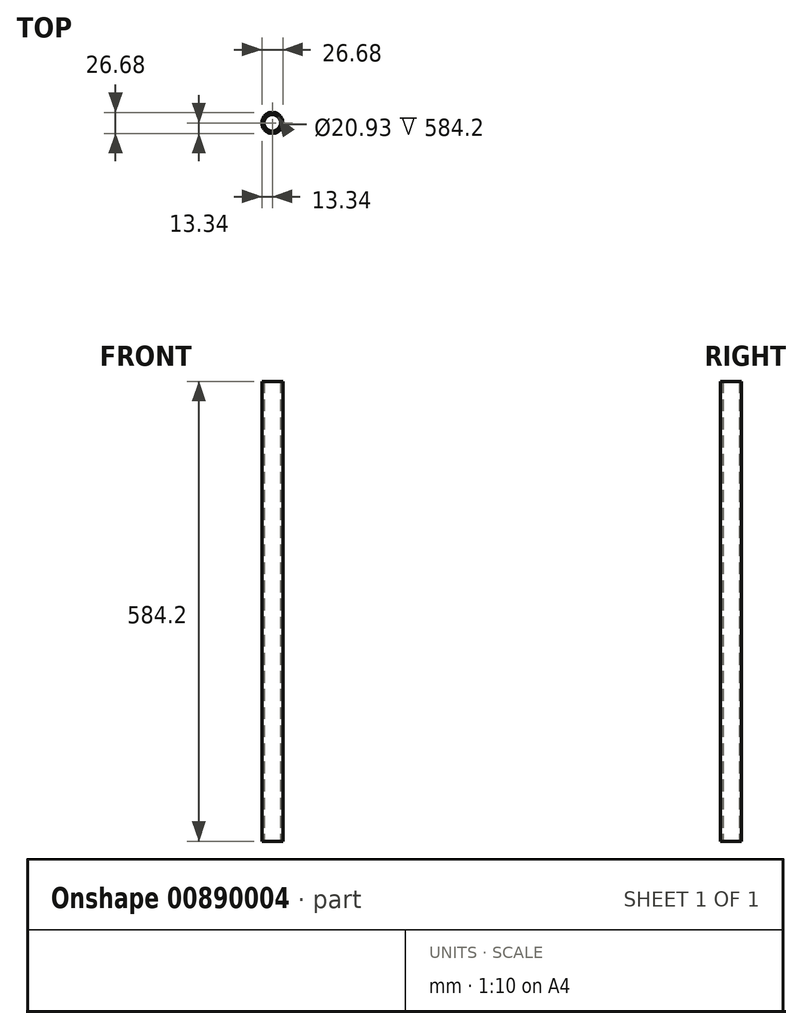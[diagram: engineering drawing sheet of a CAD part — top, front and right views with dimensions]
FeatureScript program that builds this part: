
annotation { "Feature Type Name" : "Feature", "Feature Type Description" : "" }
export const myFeature = defineFeature(function(context is Context, id is Id, definition is map)
    precondition{}
    {
        {
            var Q0;
            Q0=qCreatedBy(makeId("Top.planeOp"),FACE);
            var sketch = newSketch(context, id + "F0", { "sketchPlane" : qUnion([Q0])});
            skCircle(sketch, "E0", {"center": v(0, 0) * mm, "radius": 13.34 * mm});
            skCircle(sketch, "E1", {"center": v(0, 0) * mm, "radius": 10.46 * mm});
            skSolve(sketch);
        }
        {
            var Q0;
            Q0 = qSketchRegion(id + "F0", true);
            extrude(context, id + "F1", {"entities" : qUnion([Q0]), "depth" : 584.2 * mm, "offsetDistance" : 25.4 * mm});
        }
    });
